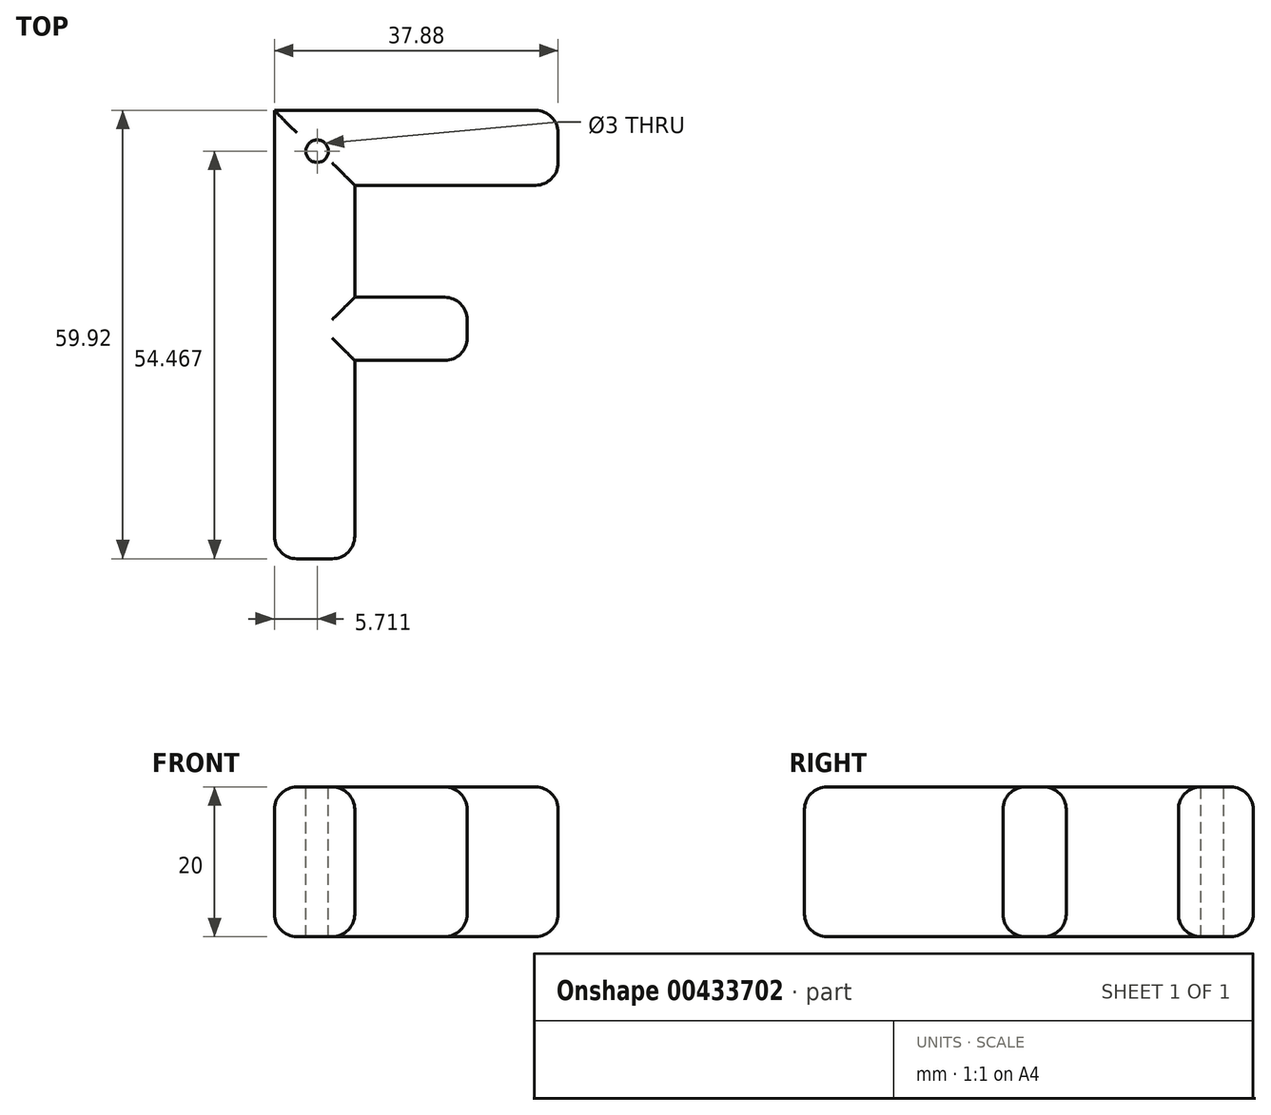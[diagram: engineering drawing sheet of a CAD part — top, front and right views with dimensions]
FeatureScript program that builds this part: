
annotation { "Feature Type Name" : "Feature", "Feature Type Description" : "" }
export const myFeature = defineFeature(function(context is Context, id is Id, definition is map)
    precondition{}
    {
        {
            var Q0;
            Q0=qCreatedBy(makeId("Top.planeOp"),FACE);
            var sketch = newSketch(context, id + "F0", { "sketchPlane" : qUnion([Q0])});
            skLineSegment(sketch, "E0", {"start": v(0, 0) * mm, "end": v(0, 20) * mm});
            skLineSegment(sketch, "E1", {"start": v(0, 20) * mm, "end": v(0, -20) * mm});
            skLineSegment(sketch, "E2", {"start": v(0, -20) * mm, "end": v(0, 13.15) * mm});
            skLineSegment(sketch, "E3", {"start": v(0, 20) * mm, "end": v(14.28, 20) * mm});
            skLineSegment(sketch, "E4", {"start": v(0, -8.5) * mm, "end": v(0, -20) * mm});
            skLineSegment(sketch, "E5", {"start": v(14.28, 30) * mm, "end": v(-10.72, 30) * mm});
            skLineSegment(sketch, "E6", {"start": v(-10.72, 30) * mm, "end": v(-10.72, -21) * mm});
            skLineSegment(sketch, "E7", {"start": v(-10.72, -21) * mm, "end": v(-10.72, 29) * mm});
            skLineSegment(sketch, "E8", {"start": v(0, -21) * mm, "end": v(0, -20) * mm});
            skLineSegment(sketch, "E9", {"start": v(14.28, 30) * mm, "end": v(27.16, 30) * mm});
            skLineSegment(sketch, "E10", {"start": v(14.28, 20) * mm, "end": v(27.16, 20) * mm});
            skLineSegment(sketch, "E11", {"start": v(27.16, 20) * mm, "end": v(27.16, 30) * mm});
            skPoint(sketch, "E12.startSnap0", {"position": v(0, -3.42) * mm});
            skLineSegment(sketch, "E13", {"start": v(15.02, -3.42) * mm, "end": v(15.02, 5.02) * mm});
            skLineSegment(sketch, "E14", {"start": v(15.02, 5.02) * mm, "end": v(0, 5.02) * mm});
            skLineSegment(sketch, "E15", {"start": v(0, -20) * mm, "end": v(0, -29.92) * mm});
            skLineSegment(sketch, "E16", {"start": v(-10.72, -29.92) * mm, "end": v(0, -29.92) * mm});
            skLineSegment(sketch, "E17", {"start": v(-10.72, -21) * mm, "end": v(-10.72, -29.92) * mm});
            skLineSegment(sketch, "E18", {"start": v(15.02, -3.42) * mm, "end": v(0, -3.42) * mm});
            skSolve(sketch);
        }
        {
            var Q0;
            Q0=makeQuery(id+"F0.imprint","IMPRINT",FACE,{"disambiguationData":[TD([[makeQuery(id+"F0.imprint","IMPRINT",EDGE,{"derivedFrom":sQuery(id+"F0.wireOp",EDGE,"E13")}),1.0]])]});
            var Q1;
            {var subQ2=sQuery(id+"F0.wireOp",EDGE,"E1");Q1=makeQuery(id+"F0.imprint","IMPRINT",FACE,{"disambiguationData":[TD([[makeQuery(id+"F0.imprint","IMPRINT",EDGE,{"derivedFrom":subQ2}),-1.0]])]});}
            extrude(context, id + "F1", {"entities" : qUnion([Q0, Q1]), "depth" : 20 * mm});
        }
        {
            var Q0;
            Q0=makeQuery(id+"F1.opExtrude","CAP_FACE",FACE,{"disambiguationData":[OSD([sQuery(id+"F0.wireOp",EDGE,"E1"),sQuery(id+"F0.wireOp",EDGE,"E2"),sQuery(id+"F0.wireOp",EDGE,"E3"),sQuery(id+"F0.wireOp",EDGE,"E4"),sQuery(id+"F0.wireOp",EDGE,"E5"),sQuery(id+"F0.wireOp",EDGE,"E6"),sQuery(id+"F0.wireOp",EDGE,"E7"),sQuery(id+"F0.wireOp",EDGE,"E9"),sQuery(id+"F0.wireOp",EDGE,"E10"),sQuery(id+"F0.wireOp",EDGE,"E11"),sQuery(id+"F0.wireOp",EDGE,"E13"),sQuery(id+"F0.wireOp",EDGE,"E14"),sQuery(id+"F0.wireOp",EDGE,"E15"),sQuery(id+"F0.wireOp",EDGE,"E16"),sQuery(id+"F0.wireOp",EDGE,"E17"),sQuery(id+"F0.wireOp",EDGE,"E18")])],"isStart":true});
            var Q1;
            Q1=makeQuery(id+"F1.opExtrude","SWEPT_FACE",FACE,{"disambiguationData":[OSD([sQuery(id+"F0.wireOp",EDGE,"E11")])]});
            var Q2;
            Q2=makeQuery(id+"F1.opExtrude","SWEPT_FACE",FACE,{"disambiguationData":[OSD([sQuery(id+"F0.wireOp",EDGE,"E13")])]});
            var Q3;
            Q3=makeQuery(id+"F1.opExtrude","CAP_EDGE",EDGE,{"disambiguationData":[OSD([sQuery(id+"F0.wireOp",EDGE,"E16")])],"isStart":false});
            var Q4;
            Q4=makeQuery(id+"F1.opExtrude","CAP_EDGE",EDGE,{"disambiguationData":[OSD([sQuery(id+"F0.wireOp",EDGE,"E16")])],"isStart":true});
            var Q5;
            Q5=makeQuery(id+"F1.opExtrude","SWEPT_EDGE",EDGE,{"disambiguationData":[OSD([sQuery(id+"F0.wireOp",EDGE,"E13"),sQuery(id+"F0.wireOp",EDGE,"E18")])]});
            var Q6;
            Q6=makeQuery(id+"F1.opExtrude","SWEPT_FACE",FACE,{"disambiguationData":[OSD([sQuery(id+"F0.wireOp",EDGE,"E16")])]});
            var Q7;
            Q7=makeQuery(id+"F1.opExtrude","CAP_EDGE",EDGE,{"disambiguationData":[OSD([sQuery(id+"F0.wireOp",EDGE,"E3"),sQuery(id+"F0.wireOp",EDGE,"E10")])],"isStart":false});
            var Q8;
            Q8=makeQuery(id+"F1.opExtrude","CAP_FACE",FACE,{"disambiguationData":[OSD([sQuery(id+"F0.wireOp",EDGE,"E1"),sQuery(id+"F0.wireOp",EDGE,"E2"),sQuery(id+"F0.wireOp",EDGE,"E3"),sQuery(id+"F0.wireOp",EDGE,"E4"),sQuery(id+"F0.wireOp",EDGE,"E5"),sQuery(id+"F0.wireOp",EDGE,"E6"),sQuery(id+"F0.wireOp",EDGE,"E7"),sQuery(id+"F0.wireOp",EDGE,"E9"),sQuery(id+"F0.wireOp",EDGE,"E10"),sQuery(id+"F0.wireOp",EDGE,"E11"),sQuery(id+"F0.wireOp",EDGE,"E13"),sQuery(id+"F0.wireOp",EDGE,"E14"),sQuery(id+"F0.wireOp",EDGE,"E15"),sQuery(id+"F0.wireOp",EDGE,"E16"),sQuery(id+"F0.wireOp",EDGE,"E17"),sQuery(id+"F0.wireOp",EDGE,"E18")])],"isStart":false});
            var Q9;
            Q9=makeQuery(id+"F1.opExtrude","SWEPT_EDGE",EDGE,{"disambiguationData":[OSD([sQuery(id+"F0.wireOp",EDGE,"E16"),sQuery(id+"F0.wireOp",EDGE,"E17")])]});
            fillet(context, id + "F2", {"entities" : qUnion([Q0, Q1, Q2, Q3, Q4, Q5, Q6, Q7, Q8, Q9]), "radius" : 3 * mm, "tangentPropagation" : true, "allowEdgeOverflow" : false});
        }
        {
            var Q0;
            Q0=makeQuery(id+"F1.opExtrude","CAP_FACE",FACE,{"disambiguationData":[OSD([sQuery(id+"F0.wireOp",EDGE,"E1"),sQuery(id+"F0.wireOp",EDGE,"E2"),sQuery(id+"F0.wireOp",EDGE,"E3"),sQuery(id+"F0.wireOp",EDGE,"E4"),sQuery(id+"F0.wireOp",EDGE,"E5"),sQuery(id+"F0.wireOp",EDGE,"E6"),sQuery(id+"F0.wireOp",EDGE,"E7"),sQuery(id+"F0.wireOp",EDGE,"E9"),sQuery(id+"F0.wireOp",EDGE,"E10"),sQuery(id+"F0.wireOp",EDGE,"E11"),sQuery(id+"F0.wireOp",EDGE,"E13"),sQuery(id+"F0.wireOp",EDGE,"E14"),sQuery(id+"F0.wireOp",EDGE,"E15"),sQuery(id+"F0.wireOp",EDGE,"E16"),sQuery(id+"F0.wireOp",EDGE,"E17"),sQuery(id+"F0.wireOp",EDGE,"E18")])],"isStart":false});
            var sketch = newSketch(context, id + "F3", { "sketchPlane" : qUnion([Q0])});
            skCircle(sketch, "E19", {"center": v(-5, 24.55) * mm, "radius": 1.5 * mm});
            skSolve(sketch);
        }
        {
            var Q0;
            Q0 = qSketchRegion(id + "F3", true);
            extrude(context, id + "F4", {"entities" : qUnion([Q0]), "operationType" : NewBodyOperationType.REMOVE, "oppositeDirection" : true, "depth" : 25 * mm});
        }
    });
